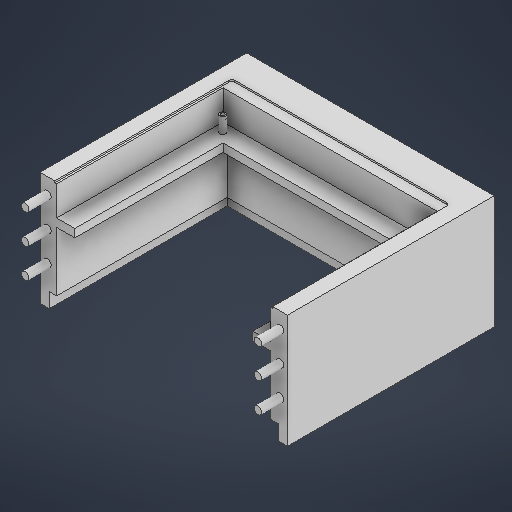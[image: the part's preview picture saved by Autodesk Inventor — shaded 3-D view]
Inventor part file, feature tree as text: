
AUTODESK INVENTOR PART (.ipt)
format: ipt  version: 2025.2 (Build 292293000, 293)  size: 387,072 bytes
history: native  units: in
note: dims shown in document units (in); Inventor stores cm internally (conversion verified against a paired STEP export)
features: sketch x13, extrude x12, split x1
ambient origin geometry x8: Origin, YZ Plane, XZ Plane, XY Plane, X Axis, Y Axis, Z Axis, Center Point
bodies: Solid1 (feature_tree)
feature tree (26):
  extrude  "Extrusion1"  Depth=6.5748in
  extrude  "Extrusion2"  Depth=5.7874in
  extrude  "Extrusion3"  Depth=0.0787in
  extrude  "Extrusion4"  Depth=0.0492in
  extrude  "Extrusion5"  Depth=5.689in
  extrude  "Extrusion8"  Depth=0.7874in TaperAngle=0.0deg
  extrude  "Extrusion9"  Depth=0.2362in
  extrude  "Extrusion10"  Depth=0.1575in
  extrude  "Extrusion11"  Depth=0.2264in
  extrude  "Extrusion12"  Depth=0.2264in
  split  "Split1"
  extrude  "Extrusion13"  Depth=0.1575in
  extrude  "Extrusion14"  Depth=0.2264in
  sketch  "Sketch1"  dims[d0=6.5748in d1=10.9843in]
  sketch  "Sketch2"  dims[d2=1.0472in d3=0.0in d4=5.7874in]
  sketch  "Sketch3"  dims[d5=9.4094in d6=0.0787in]
  sketch  "Sketch4"  dims[d7=0.0433in d8=0.0in d9=0.0492in]
  sketch  "Sketch5"  dims[d10=0.0657in d11=5.689in]
  sketch  "Sketch8"  dims[d12=9.0591in d13=0.7874in d14=0.0in]
  sketch  "Sketch9"  dims[d15=0.1575in d16=0.2362in]
  sketch  "Sketch10"  dims[d17=0.2264in d18=0.1575in]
  sketch  "Sketch12"  dims[d19=0.2362in d20=0.2264in]
  sketch  "Sketch13"  dims[d21=0.1575in d22=0.2264in]
  sketch  "Sketch14"  dims[d23=0.2362in d24=0.1575in]
  sketch  "Sketch16"  dims[d25=0.2362in d26=0.2264in]
  sketch  "Sketch17"  dims[d27=0.4055in d28=0.0in d29=0.0984in d30=0.0984in d31=0.0984in d32=0.0984in d33=0.4055in d34=0.0in d35=0.2165in d36=0.0in d49=0.1378in d50=0.1378in d51=0.1378in d52=0.1378in d53=0.5433in d54=0.0in d55=4.7244in d56=7.874in d57=0.2283in d58=0.0in d59=1.5748in d60=0.0in d67=5.689in d68=9.0591in d69=0.1969in d70=0.1969in d71=9.4528in d72=0.1969in d73=0.1969in d74=9.4528in d75=0.3937in d76=0.0in d77=0.0984in d78=0.2362in d79=0.2362in d80=0.0984in d81=0.2362in d82=0.2362in d83=0.0984in d84=0.2362in d85=0.2362in d86=0.2362in d87=0.2362in d88=0.3937in d89=0.0in d90=6.5812in d91=0.0in d92=0.1969in d95=0.1969in d97=0.1969in d99=0.1969in d100=0.5906in d101=0.0in d47=0.0197in d48=0.0344in]
